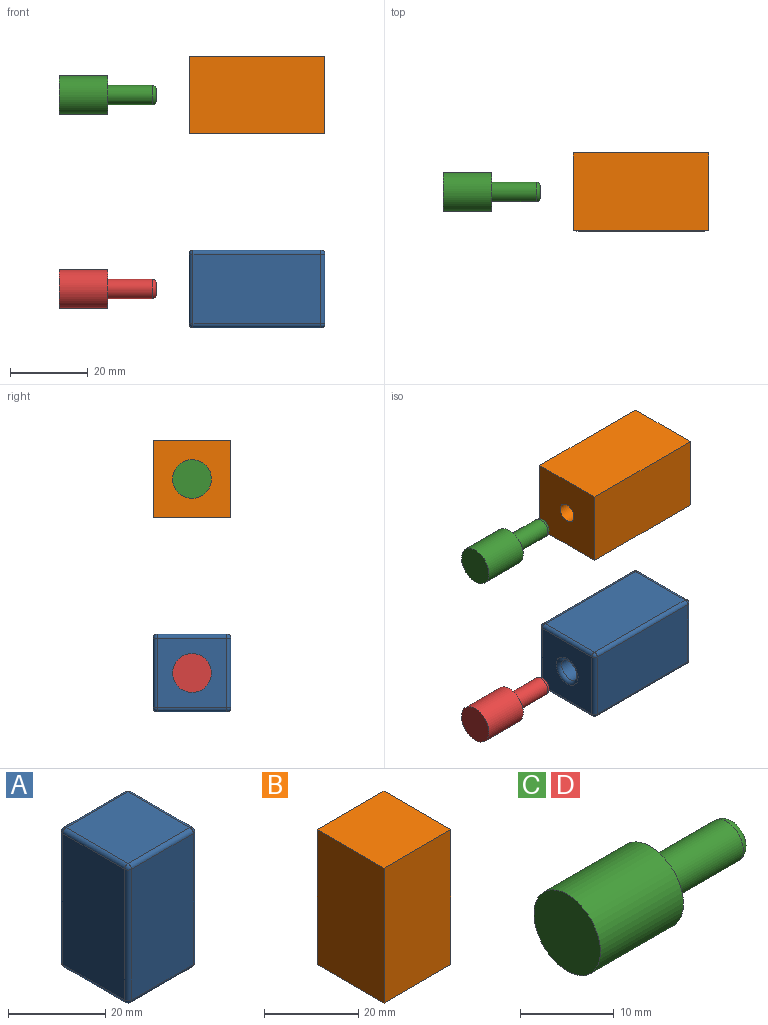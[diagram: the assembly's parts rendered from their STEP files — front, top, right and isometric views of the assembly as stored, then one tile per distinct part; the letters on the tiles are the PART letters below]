
ASSEMBLY  parts=4 mates=7
PART A: 29 faces, bbox 20x20x35 mm
  f0: plane 33x18mm, normal (0,-1,0), area 594mm2, adj f17,f22,f25,f28
  f1: plane 33x18mm, normal (1,0,0), area 594mm2, adj f14,f23,f24,f28
  f2: plane 33x18mm, normal (0,1,0), area 594mm2, adj f9,f13,f14,f15
  f3: plane 33x18mm, normal (-1,0,0), area 594mm2, adj f9,f12,f16,f17
  f4: plane 18x18mm, normal (0,0,1), area 324mm2, adj f12,f13,f22,f23
  f5: plane 18x18mm, normal (0,0,-1), area 273.7mm2, adj f8,f15,f16,f24,f25
  f6: cylinder r=3mm len=24mm, axis (0,0,-1), area 452.4mm2, adj f7,f8
  f7: plane 6x6mm, normal (0,0,-1), area 28.3mm2, adj f6
  f8: torus R=4mm, axis (0,0,1), area 33.2mm2, adj f5,f6
  f9: cylinder r=1mm len=33mm, axis (0,0,1), area 51.8mm2, adj f2,f3,f10,f11
  f10: sphere r=1mm, area 1.6mm2, adj f9,f12,f13
  f11: sphere r=1mm, area 1.6mm2, adj f9,f15,f16
  f12: cylinder r=1mm len=18mm, axis (0,1,0), area 28.3mm2, adj f3,f4,f10,f18
  f13: cylinder r=1mm len=18mm, axis (1,0,0), area 28.3mm2, adj f2,f4,f10,f19
  f14: cylinder r=1mm len=33mm, axis (0,0,-1), area 51.8mm2, adj f1,f2,f19,f20
  f15: cylinder r=1mm len=18mm, axis (-1,0,0), area 28.3mm2, adj f2,f5,f11,f20
  f16: cylinder r=1mm len=18mm, axis (0,-1,0), area 28.3mm2, adj f3,f5,f11,f21
  f17: cylinder r=1mm len=33mm, axis (0,0,-1), area 51.8mm2, adj f0,f3,f18,f21
  f18: sphere r=1mm, area 1.6mm2, adj f12,f17,f22
  f19: sphere r=1mm, area 1.6mm2, adj f13,f14,f23
  f20: sphere r=1mm, area 1.6mm2, adj f14,f15,f24
  f21: sphere r=1mm, area 1.6mm2, adj f16,f17,f25
  f22: cylinder r=1mm len=18mm, axis (-1,0,0), area 28.3mm2, adj f0,f4,f18,f26
  f23: cylinder r=1mm len=18mm, axis (0,-1,0), area 28.3mm2, adj f1,f4,f19,f26
  f24: cylinder r=1mm len=18mm, axis (0,1,0), area 28.3mm2, adj f1,f5,f20,f27
  f25: cylinder r=1mm len=18mm, axis (1,0,0), area 28.3mm2, adj f0,f5,f21,f27
  f26: sphere r=1mm, area 1.6mm2, adj f22,f23,f28
  f27: sphere r=1mm, area 1.6mm2, adj f24,f25,f28
  f28: cylinder r=1mm len=33mm, axis (0,0,1), area 51.8mm2, adj f0,f1,f26,f27
PART B: 8 faces, bbox 20x20x35 mm
  f0: plane 35x20mm, normal (0,-1,0), area 700mm2, adj f1,f3,f4,f5
  f1: plane 35x20mm, normal (1,0,0), area 700mm2, adj f0,f2,f4,f5
  f2: plane 35x20mm, normal (0,1,0), area 700mm2, adj f1,f3,f4,f5
  f3: plane 35x20mm, normal (-1,0,0), area 700mm2, adj f0,f2,f4,f5
  f4: plane 20x20mm, normal (0,0,1), area 400mm2, adj f0,f1,f2,f3
  f5: plane 20x20mm, normal (0,0,-1), area 380.4mm2, adj f0,f1,f2,f3,f6
  f6: cylinder r=2.5mm len=25mm, axis (0,0,-1), area 392.7mm2, adj f5,f7
  f7: plane 5x5mm, normal (0,0,-1), area 19.6mm2, adj f6
PART C: 6 faces, bbox 25x10x10 mm
  f0: plane 3x3mm, normal (1,0,0), area 7.1mm2, adj f5
  f1: cylinder r=2.5mm len=11.5mm, axis (1,0,0), area 180.6mm2, adj f2,f5
  f2: plane 10x10mm, normal (1,0,0), area 58.9mm2, adj f1,f3
  f3: cylinder r=5mm len=12.5mm, axis (1,0,0), area 392.7mm2, adj f2,f4
  f4: plane 10x10mm, normal (-1,0,0), area 78.5mm2, adj f3
  f5: torus R=1.5mm, axis (1,0,0), area 21.1mm2, adj f0,f1
PART D: same geometry as C
PLACE A rot(axis=(0.71,0,0.71),180deg) t=(18.57,-5.12,-55.26)mm
PLACE B rot(axis=(0.71,0,0.71),180deg) t=(18.57,-5.12,-5.26)mm fixed
PLACE C rot(axis=(-1,0,0),147.1deg) t=(10.05,-5.12,-5.26)mm
PLACE D rot(axis=(-1,0,0),137.4deg) t=(10.05,-5.12,-55.26)mm
MATE planar A.f2 <-> B.f2  axis (0,-1,0) through (36.07,-15.12,-55.26)mm
MATE planar C.f1 <-> D.f1  axis (-1,0,0) through (-14.95,-5.12,-5.26)mm
MATE planar A.f4 <-> B.f6  axis (1,0,0) through (53.57,-5.12,-46.26)mm
MATE fastened B.f2 <-> A.f2  axis (0,-1,0) through (36.07,-15.12,-5.26)mm
MATE parallel B.f5 <-> C.f1  axis (-1,0,0) through (18.57,-15.12,-5.26)mm
MATE cylindrical C.f1 <-> B.f6  axis (1,0,0) through (3.3,-5.12,-5.26)mm
MATE cylindrical A.f6 <-> D.f1  axis (1,0,0) through (19.57,-5.12,-55.26)mm
